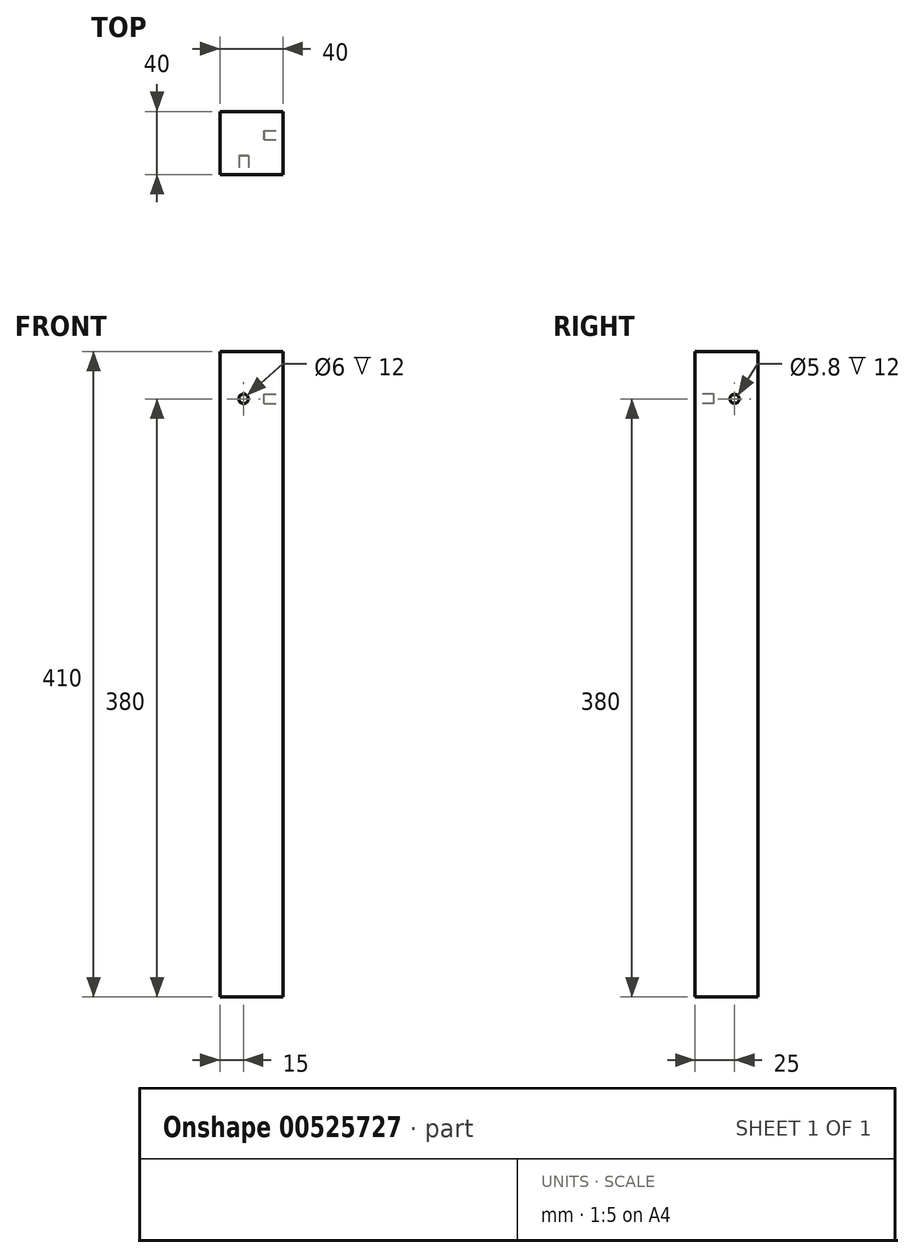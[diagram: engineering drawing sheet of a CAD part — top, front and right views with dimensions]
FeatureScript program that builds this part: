
annotation { "Feature Type Name" : "Feature", "Feature Type Description" : "" }
export const myFeature = defineFeature(function(context is Context, id is Id, definition is map)
    precondition{}
    {
        {
            var Q0;
            Q0=qCreatedBy(makeId("Top.planeOp"),FACE);
            var sketch = newSketch(context, id + "F0", { "sketchPlane" : qUnion([Q0])});
            skLineSegment(sketch, "E0.bottom", {"start": v(0, 0) * mm, "end": v(40, 0) * mm});
            skLineSegment(sketch, "E0.top", {"start": v(0, 40) * mm, "end": v(40, 40) * mm});
            skLineSegment(sketch, "E0.left", {"start": v(0, 0) * mm, "end": v(0, 40) * mm});
            skLineSegment(sketch, "E0.right", {"start": v(40, 0) * mm, "end": v(40, 40) * mm});
            skSolve(sketch);
        }
        {
            var Q0;
            Q0=qSketchRegion(id+"F0",true);
            extrude(context, id + "F1", {"entities" : qUnion([Q0]), "depth" : 410 * mm, "offsetDistance" : 25 * mm});
        }
        {
            var Q0;
            Q0=makeQuery(id+"F1.opExtrude","SWEPT_FACE",FACE,{"disambiguationData":[OSD([sQuery(id+"F0.wireOp",EDGE,"E0.bottom")])]});
            var sketch = newSketch(context, id + "F2", { "sketchPlane" : qUnion([Q0])});
            skCircle(sketch, "E1", {"center": v(15, 380) * mm, "radius": 3 * mm});
            skSolve(sketch);
        }
        {
            var Q0;
            Q0=qSketchRegion(id+"F2",true);
            extrude(context, id + "F3", {"entities" : qUnion([Q0]), "operationType" : NewBodyOperationType.REMOVE, "oppositeDirection" : true, "depth" : 12 * mm, "offsetDistance" : 25 * mm});
        }
        {
            var Q0;
            Q0=makeQuery(id+"F1.opExtrude","SWEPT_FACE",FACE,{"disambiguationData":[OSD([sQuery(id+"F0.wireOp",EDGE,"E0.right")])]});
            var sketch = newSketch(context, id + "F4", { "sketchPlane" : qUnion([Q0])});
            skCircle(sketch, "E2", {"center": v(25, 380) * mm, "radius": 2.9 * mm});
            skSolve(sketch);
        }
        {
            var Q0;
            Q0=qSketchRegion(id+"F4",true);
            extrude(context, id + "F5", {"entities" : qUnion([Q0]), "operationType" : NewBodyOperationType.REMOVE, "oppositeDirection" : true, "depth" : 12 * mm, "offsetDistance" : 25 * mm});
        }
    });
